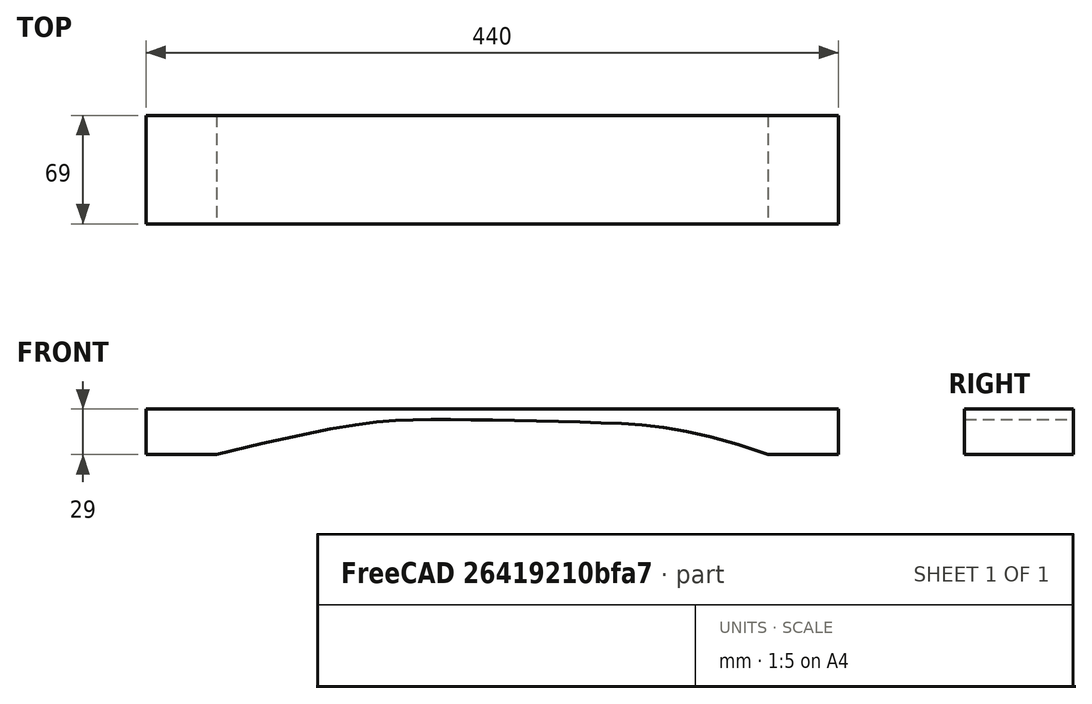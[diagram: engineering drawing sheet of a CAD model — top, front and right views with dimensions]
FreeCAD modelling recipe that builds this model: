
FCSTD DOCUMENT  (FreeCAD 0.20R29410 (Git))
Label: Single_Bar4
License: All rights reserved
LicenseURL: http://en.wikipedia.org/wiki/All_rights_reserved
objects: Sketcher::SketchObject×1, Part::Extrusion×1, Fem::FemSolverObjectPython×1, App::MaterialObjectPython×1, Fem::ConstraintDisplacement×1, Fem::FemMeshShapeNetgenObject×1, Fem::FemAnalysis×1
note: 2 computed .brp shape members not serialized (recipe doc carries the construction recipe); baked Part::Feature solids carry a one-line shape summary decoded from their .brp

FEATURE [Sketcher::SketchObject] Sketch
  FullyConstrained = true
  Placement = pos=(0,0,0) rot=(1,0,0;1.5708rad)
  sketch-geometry (12):
    g0: LineSegment StartX=44.78 StartY=0 StartZ=0 EndX=0 EndY=0 EndZ=0
    g1: LineSegment StartX=0 StartY=0 StartZ=0 EndX=0 EndY=29 EndZ=0
    g2: LineSegment StartX=0 StartY=29 StartZ=0 EndX=440 EndY=29 EndZ=0
    g3: LineSegment StartX=440 StartY=29 StartZ=0 EndX=440 EndY=0 EndZ=0
    g4: LineSegment StartX=440 StartY=0 StartZ=0 EndX=395.22 EndY=0 EndZ=0
    g5-g10: Circle x6 (B-spline internal-alignment scaffolding for g11; pole/knot coordinates omitted)
    g11: BSplineCurve PolesCount=6 KnotsCount=4 Degree=3 IsPeriodic=0
  constraints (38):
    c: DistanceX(g0) = 0
    c: DistanceY(g0) = 0
    c: Distance(g1,g1) = 29
    c: Distance(g2,g2) = 440
    c: DistanceX(g0,g0) = 44.78
    c: DistanceX(g4,g4) = 44.78
    c: Horizontal(g0)
    c: Vertical(g1)
    c: Horizontal(g2)
    c: Vertical(g3)
    c: Horizontal(g4)
    c: Equal(g3,g1)
    c: Coincident(g0,g1)
    c: Coincident(g1,g2)
    c: Coincident(g2,g3)
    c: Coincident(g3,g4)
    c: DistanceX(g6) = 343.71
    c: DistanceY(g6) = 18.63
    c: DistanceX(g7) = 284.82
    c: DistanceY(g7) = 20.42
    c: DistanceX(g8) = 168.2
    c: DistanceY(g8) = 23.47
    c: DistanceX(g9) = 126.8
    c: DistanceY(g9) = 20.13
    c: Weight(g5) = 1
    c: InternalAlignment(g5,g11)
    c: Weight(g6) = 1
    c: InternalAlignment(g6,g11)
    c: Weight(g7) = 1
    c: InternalAlignment(g7,g11)
    c: Weight(g8) = 1
    c: InternalAlignment(g8,g11)
    c: Weight(g9) = 1
    c: InternalAlignment(g9,g11)
    c: Weight(g10) = 1
    c: InternalAlignment(g10,g11)
    c: Coincident(g4,g11)
    c: Coincident(g0,g11)
FEATURE [Part::Extrusion] Bar
  Base = -> Sketch
  Dir = (0,-1,-3e-16)
  DirMode = 2
  FaceMakerClass = Part::FaceMakerBullseye
  LengthFwd = 69
  LengthRev = 0
  Solid = true
  Symmetric = false
FEATURE [Fem::FemSolverObjectPython] SolverCcxTools  # FEM object (typed FeaturePython)
  AnalysisType = 0
  BeamShellResultOutput3D = false
  BucklingFactors = 1
  EigenmodeHighLimit = 20000
  EigenmodeLowLimit = 20
  EigenmodesCount = 12
  GeometricalNonlinearity = 0
  IterationsControlParameterCutb = 0.25,0.5,0.75,0.85,,,1.5,
  IterationsControlParameterIter = 4,8,9,200,10,400,,200,,
  IterationsControlParameterTimeUse = false
  IterationsThermoMechMaximum = 2000
  IterationsUserDefinedIncrementations = false
  IterationsUserDefinedTimeStepLength = false
  MaterialNonlinearity = 0
  MatrixSolverType = 0
  SplitInputWriter = false
  ThermoMechSteadyState = false
  TimeEnd = 1
  TimeInitialStep = 0.01
FEATURE [App::MaterialObjectPython] MaterialSolid  # material (typed FeaturePython)
  Category = 0
  Material = CompressiveStrength=7800 kPa,Density=670 kg/m^3,Name=White European Oak,PoissonRatio=0.37,ShearModulus=11.6 MPa,UltimateTensileStrength=97.1 MPa,+1 more (map truncated)
FEATURE [Fem::ConstraintDisplacement] FemConstraintDisplacement
  NormalDirection = (0,3e-16,-1)
  Normals = (116) [(0,3.33067e-16,-1),(0,3.33067e-16,-1),(0,3.33067e-16,-1),(0,3.33067e-16,-1),(0,3.33067e-16,-1),(0,3.33067e-16,-1),(0,3.33067e-16,-1),+109 more]
  Points = (116) [(44.78,-69,-2.29816e-14),(29.8533,-69,-2.29816e-14),(14.9267,-69,-2.29816e-14),(0,-69,-2.29816e-14),(44.78,-46,-1.53211e-14),+111 more]
  References = -> [Bar]
  rotxFix = false
  rotxFree = true
  rotyFix = false
  rotyFree = true
  rotzFix = false
  rotzFree = true
  xDisplacement = 0
  xFix = false
  xFree = true
  xRotation = 0
  yDisplacement = 0
  yFix = true
  yFree = false
  yRotation = 0
  zDisplacement = 0
  zFix = false
  zFree = true
  zRotation = 0
FEATURE [Fem::FemMeshShapeNetgenObject] FEMMeshNetgen
  Fineness = 4
  GrowthRate = 0.3
  MaxSize = 10
  NbSegsPerEdge = 1
  NbSegsPerRadius = 2
  Optimize = true
  SecondOrder = true
  Shape = -> Bar
FEATURE [Fem::FemAnalysis] Analysis
  Group = -> [SolverCcxTools,MaterialSolid,FemConstraintDisplacement,FEMMeshNetgen]
